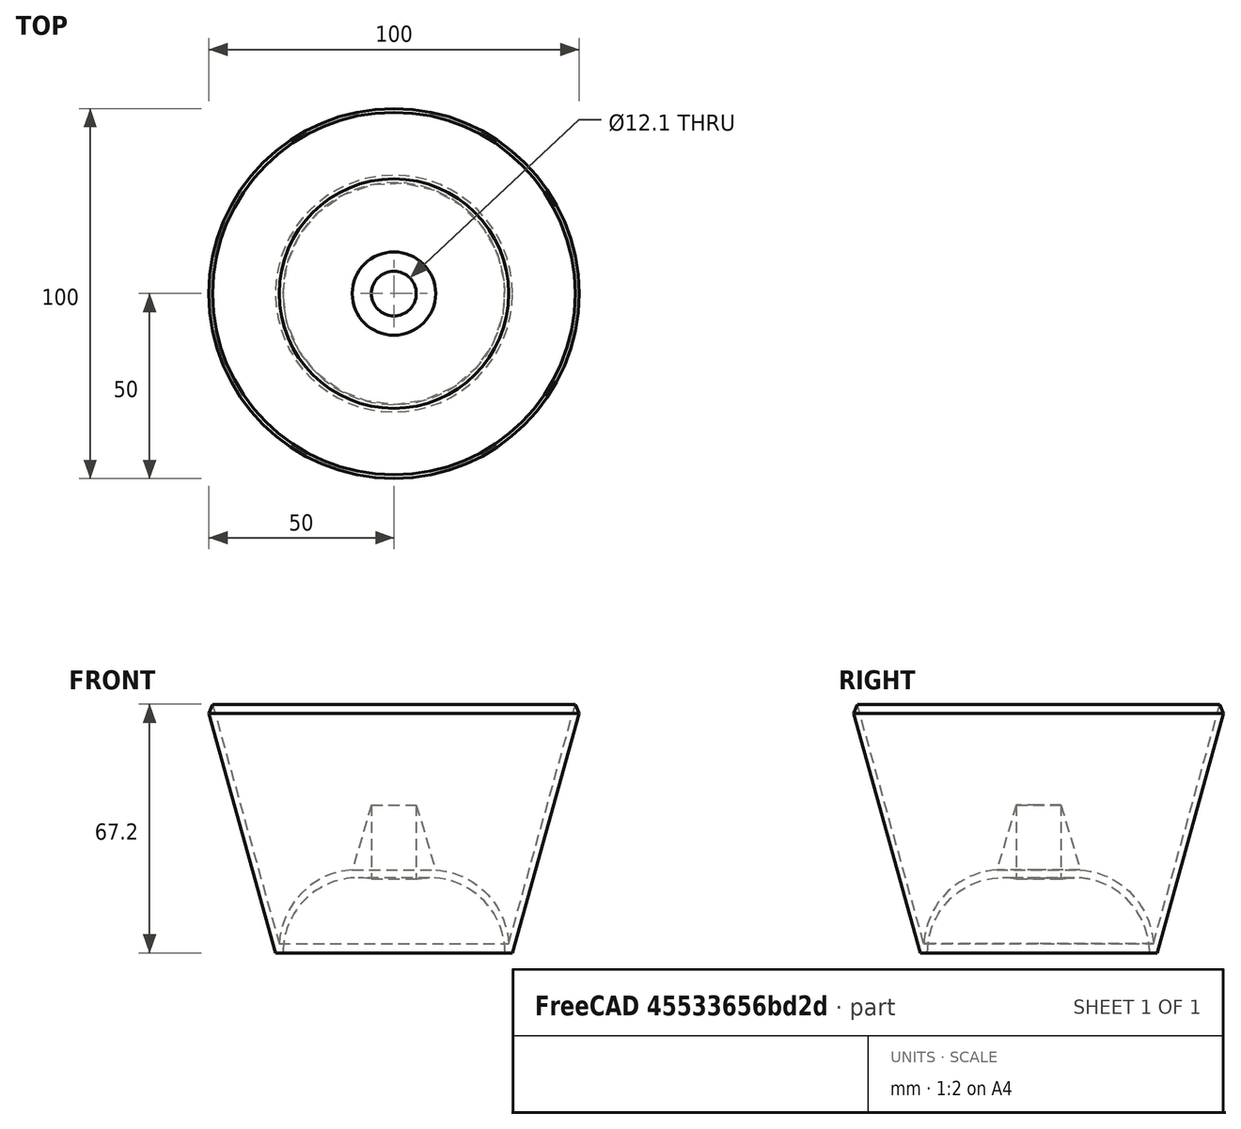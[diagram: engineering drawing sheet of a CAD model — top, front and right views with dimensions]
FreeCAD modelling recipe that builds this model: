
FCSTD DOCUMENT  (FreeCAD 0.19R)
Label: bowl
License: All rights reserved
LicenseURL: http://en.wikipedia.org/wiki/All_rights_reserved
objects: Sketcher::SketchObject×1, PartDesign::Revolution×1, PartDesign::Body×1
note: 4 computed .brp shape members not serialized (recipe doc carries the construction recipe); baked Part::Feature solids carry a one-line shape summary decoded from their .brp

FEATURE [Sketcher::SketchObject] Sketch
  FullyConstrained = false
  MapMode = 5
  Placement = pos=(0,0,0) rot=(1,0,0;1.5708rad)
  Support = -> [XZ_Plane]
  sketch-geometry (8):
    g0: LineSegment StartX=-50 StartY=34.7391 StartZ=0 EndX=-32 EndY=-30 EndZ=0
    g1: LineSegment StartX=-32 StartY=-30 StartZ=0 EndX=-30 EndY=-30 EndZ=0
    g2: LineSegment StartX=-6.05 StartY=10 StartZ=0 EndX=-6.05 EndY=-10 EndZ=0
    g3: LineSegment StartX=-6.05 StartY=10 StartZ=0 EndX=-11.266 EndY=-7.54787 EndZ=0
    g4: ArcOfCircle CenterX=-9.67515 CenterY=-29.9989 CenterZ=0 NormalX=0 NormalY=0 NormalZ=1 AngleXU=0 Radius=20.3248 StartAngle=1.39148 EndAngle=3.14164
    g5: LineSegment StartX=-50 StartY=34.7391 StartZ=0 EndX=-49 EndY=37.1951 EndZ=0
    g6: LineSegment StartX=-49 StartY=37.1951 StartZ=0 EndX=-31 EndY=-27.544 EndZ=0
    g7: ArcOfCircle CenterX=-9.80593 CenterY=-28.7245 CenterZ=0 NormalX=0 NormalY=0 NormalZ=1 AngleXU=0 Radius=21.2269 StartAngle=1.63963 EndAngle=3.08595
  constraints (19):
    c: Coincident(g1,g0)
    c: Vertical(g2)
    c: Coincident(g3,g2)
    c: Coincident(g4,g1)
    c: Coincident(g4,g2)
    c: DistanceX(g1,g-1) = 30
    c: DistanceX(g2,g-1) = 6.05
    c: DistanceX(g0,g-1) = 50
    c: DistanceY(g2,g2) = 20
    c: DistanceY(g2,g-1) = 10
    c: DistanceY(g1,g2) = 20
    c: Distance(g1) = 2
    c: Coincident(g5,g0)
    c: Coincident(g6,g5)
    c: Parallel(g0,g6)
    c: DistanceX(g5,g5) = 1
    c: Equal(g6,g0)
    c: Coincident(g7,g6)
    c: Coincident(g7,g3)
FEATURE [PartDesign::Revolution] Revolution
  Angle = 360
  Axis = (0,2e-16,1)
  Base = (0,0,0)
  Placement = pos=(0,0,0) rot=(1,0,0;1.5708rad)
  Profile = -> Sketch
  ReferenceAxis = -> Sketch [V_Axis]
FEATURE [PartDesign::Body] Body
  Group = -> [Sketch,Revolution]
  Origin = -> Origin
  Tip = -> Revolution
